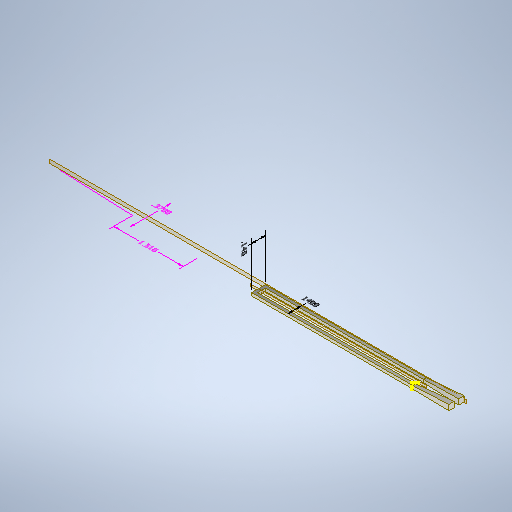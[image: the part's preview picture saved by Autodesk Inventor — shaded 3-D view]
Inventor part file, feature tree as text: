
AUTODESK INVENTOR PART (.ipt)
format: ipt  version: 2025.2 (Build 292293000, 293)  size: 307,200 bytes
history: native  units: in
note: dims shown in document units (in); Inventor stores cm internally (conversion verified against a paired STEP export)
features: other x6, plane x4, sketch x4, sweep x1, loft x1, mirror x1, projected_geometry x1
ambient origin geometry x8: Origin, YZ Plane, XZ Plane, XY Plane, X Axis, Y Axis, Z Axis, Center Point
bodies: Solid1 (feature_tree)
feature tree (18):
  other  "Annotations"
  sweep  "Sweep1"
  plane  "Work Plane1"
  plane  "Work Plane2"
  plane  "Work Plane4"
  sketch  "Sketch15"  dims[d86=-0.1175in]
  sketch  "Sketch16"  dims[d89=0.1in d90=0.0in d91=0.0in d92=0.0in d98=0.03in d99=0.03in d100=0.055in d102=0.055in d104=0.0in d109=0.0in d110=90.0deg d111=0.0in d112=90.0deg d116=-0.07in d113=0.0in d114=0.3937in d115=0.14in d117=0.086in d118=0.3123in d119=0.14in d42=0.2341in d43=0.169in d44=0.37in d48=0.2141in d49=0.2512in d50=1.51in]
  loft  "Loft3"
  plane  "Work Plane5"
  mirror  "Mirror3"
  sketch  "Sketch1"  dims[d6=0.0in d7=0.0in d11=0.375in d19=-0.25in]
  sketch  "Sketch2"  dims[d69=1.625in d70=1.625in]
  projected_geometry  "Projected Loop1"
  other  "Edges4"
  other  "Linear Dimension 1"
  other  "Linear Dimension 3"
  other  "Linear Dimension 4"
  other  "Linear Dimension 5"
